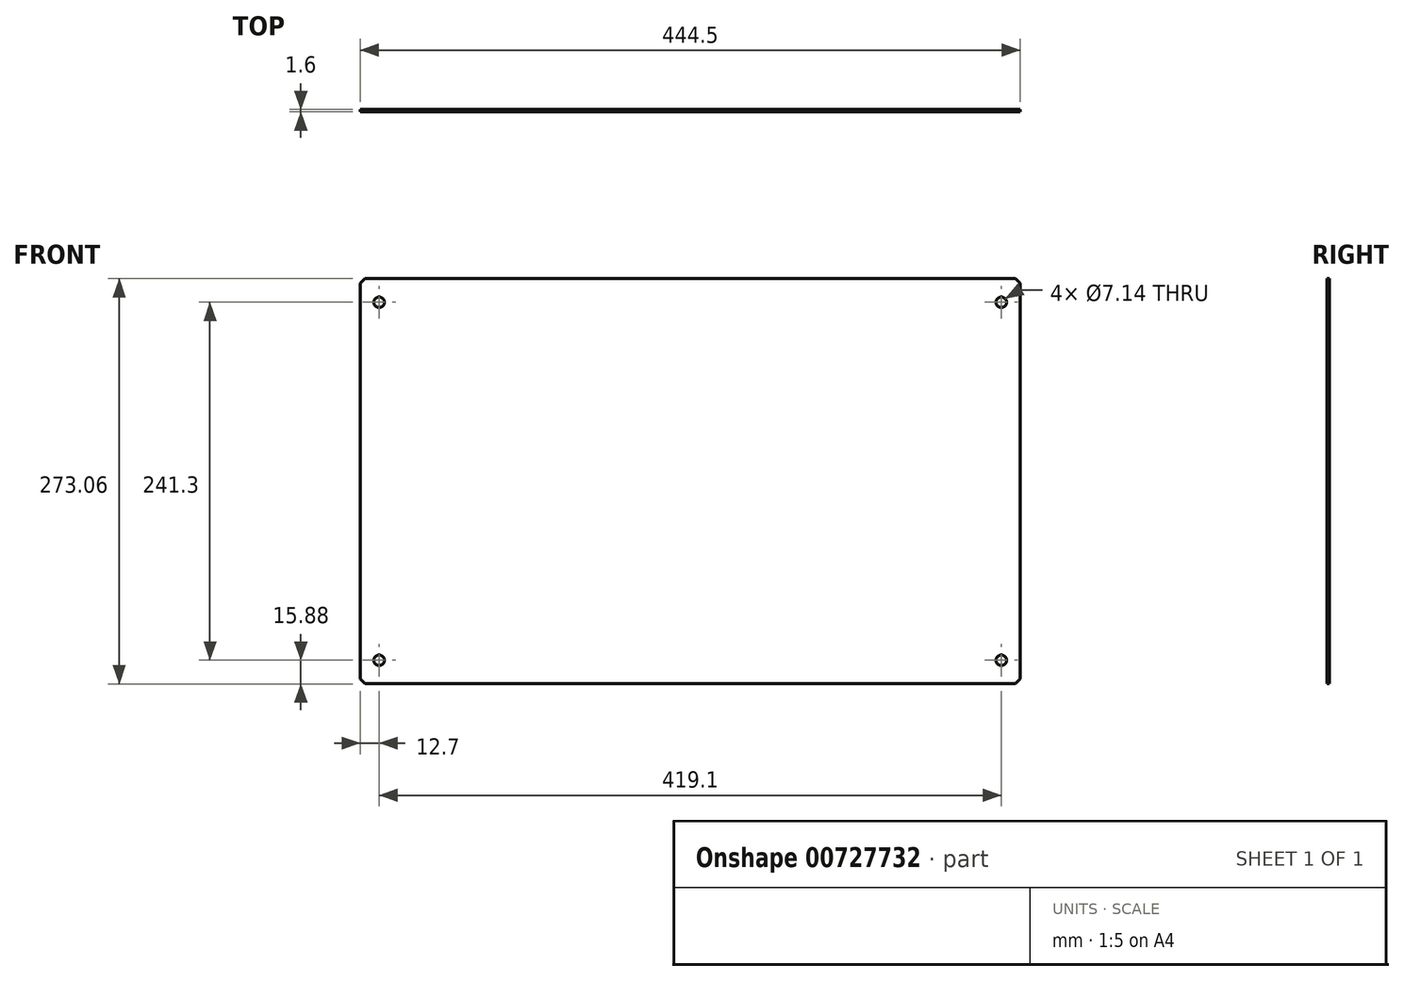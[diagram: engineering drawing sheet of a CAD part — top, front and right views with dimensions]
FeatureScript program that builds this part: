
annotation { "Feature Type Name" : "Feature", "Feature Type Description" : "" }
export const myFeature = defineFeature(function(context is Context, id is Id, definition is map)
    precondition{}
    {
        {
            var Q0;
            Q0=qCreatedBy(makeId("Front.planeOp"),FACE);
            var sketch = newSketch(context, id + "F0", { "sketchPlane" : qUnion([Q0])});
            skLineSegment(sketch, "E0.bottom", {"start": v(-222.25, 136.53) * mm, "end": v(222.25, 136.52) * mm});
            skLineSegment(sketch, "E0.top", {"start": v(-222.25, -136.52) * mm, "end": v(222.25, -136.53) * mm});
            skLineSegment(sketch, "E0.left", {"start": v(-222.25, 136.53) * mm, "end": v(-222.25, -136.53) * mm});
            skLineSegment(sketch, "E0.right", {"start": v(222.25, 136.53) * mm, "end": v(222.25, -136.53) * mm});
            skLineSegment(sketch, "E1", {"start": v(0, 136.53) * mm, "end": v(0, 0) * mm, "construction": true});
            skLineSegment(sketch, "E2", {"start": v(0, 0) * mm, "end": v(-222.25, 0) * mm, "construction": true});
            skSolve(sketch);
        }
        {
            var Q0;
            Q0=qSketchRegion(id+"F0",true);
            extrude(context, id + "F1", {"entities" : qUnion([Q0]), "depth" : 1.6 * mm, "offsetDistance" : 25.4 * mm});
        }
        {
            var Q0;
            Q0=makeQuery(id+"F1.opExtrude","SWEPT_EDGE",EDGE,{"disambiguationData":[OSD([sQuery(id+"F0.wireOp",EDGE,"E0.bottom"),sQuery(id+"F0.wireOp",EDGE,"E0.left")])]});
            var Q1;
            Q1=makeQuery(id+"F1.opExtrude","SWEPT_EDGE",EDGE,{"disambiguationData":[OSD([sQuery(id+"F0.wireOp",EDGE,"E0.top"),sQuery(id+"F0.wireOp",EDGE,"E0.left")])]});
            var Q2;
            Q2=makeQuery(id+"F1.opExtrude","SWEPT_EDGE",EDGE,{"disambiguationData":[OSD([sQuery(id+"F0.wireOp",EDGE,"E0.top"),sQuery(id+"F0.wireOp",EDGE,"E0.right")])]});
            var Q3;
            Q3=makeQuery(id+"F1.opExtrude","SWEPT_EDGE",EDGE,{"disambiguationData":[OSD([sQuery(id+"F0.wireOp",EDGE,"E0.bottom"),sQuery(id+"F0.wireOp",EDGE,"E0.right")])]});
            chamfer(context, id + "F2", {"entities" : qUnion([Q0, Q1, Q2, Q3]), "width" : 3.17 * mm, "tangentPropagation" : true});
        }
        {
            var Q0;
            Q0=makeQuery(id+"F1.opExtrude","CAP_FACE",FACE,{"disambiguationData":[OSD([sQuery(id+"F0.wireOp",EDGE,"E0.bottom"),sQuery(id+"F0.wireOp",EDGE,"E0.top"),sQuery(id+"F0.wireOp",EDGE,"E0.left"),sQuery(id+"F0.wireOp",EDGE,"E0.right")])],"isStart":false});
            var sketch = newSketch(context, id + "F3", { "sketchPlane" : qUnion([Q0])});
            skLineSegment(sketch, "E3.bottom", {"start": v(-209.55, 120.65) * mm, "end": v(209.55, 120.65) * mm, "construction": true});
            skLineSegment(sketch, "E3.top", {"start": v(-209.55, -120.65) * mm, "end": v(209.55, -120.65) * mm, "construction": true});
            skLineSegment(sketch, "E3.left", {"start": v(-209.55, 120.65) * mm, "end": v(-209.55, -120.65) * mm, "construction": true});
            skLineSegment(sketch, "E3.right", {"start": v(209.55, 120.65) * mm, "end": v(209.55, -120.65) * mm, "construction": true});
            skLineSegment(sketch, "E4", {"start": v(0, 120.65) * mm, "end": v(0, 0) * mm, "construction": true});
            skLineSegment(sketch, "E5", {"start": v(0, 0) * mm, "end": v(-209.55, 0) * mm, "construction": true});
            skSolve(sketch);
        }
        {
            var Q0;
            Q0=sQuery(id+"F3.wireOp",VERTEX,"E3.bottom.start");
            var Q1;
            Q1=sQuery(id+"F3.wireOp",VERTEX,"E3.right.start");
            var Q2;
            Q2=sQuery(id+"F3.wireOp",VERTEX,"E3.right.end");
            var Q3;
            Q3=sQuery(id+"F3.wireOp",VERTEX,"E3.left.end");
            var Q4;
            Q4=makeQuery(id+"F1.opExtrude","SWEPT_BODY",BODY,{"disambiguationData":[OSD([sQuery(id+"F0.wireOp",EDGE,"E0.bottom"),sQuery(id+"F0.wireOp",EDGE,"E0.top"),sQuery(id+"F0.wireOp",EDGE,"E0.left"),sQuery(id+"F0.wireOp",EDGE,"E0.right")])]});
            hole(context, id + "F4", {"style" : HoleStyle.SIMPLE, "endStyle" : HoleEndStyle.THROUGH, "holeDiameter" : 7.14 * mm, "majorDiameter" : 6.35 * mm, "isTappedThrough" : true, "tappedDepth" : 12.7 * mm, "tapClearance" : 3, "locations" : qUnion([Q0, Q1, Q2, Q3]), "scope" : qUnion([Q4])});
        }
    });
